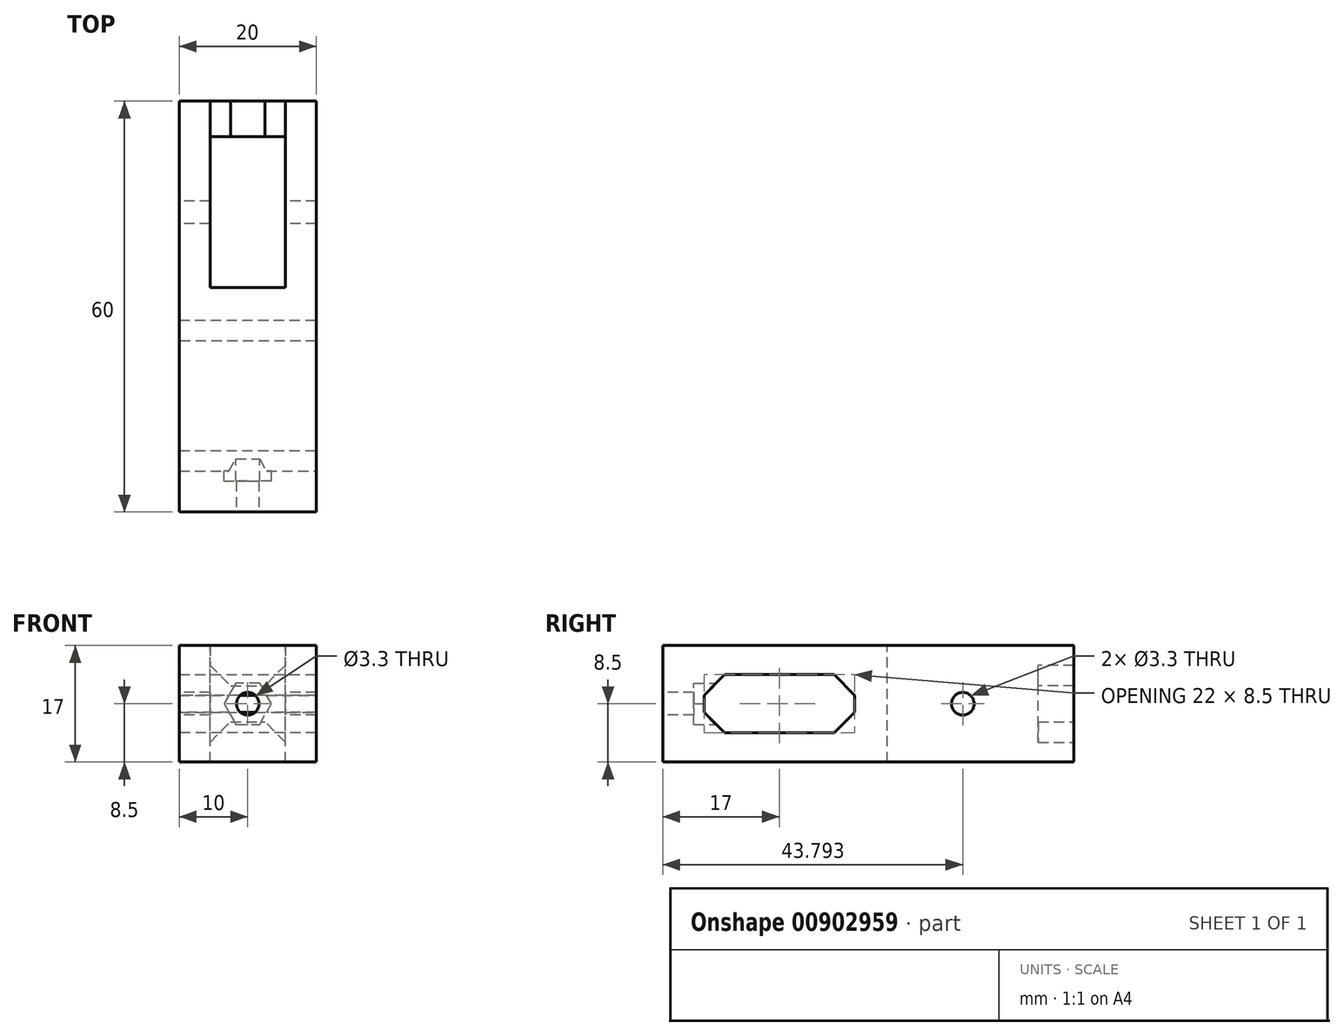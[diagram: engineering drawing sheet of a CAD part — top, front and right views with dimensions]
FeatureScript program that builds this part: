
annotation { "Feature Type Name" : "Feature", "Feature Type Description" : "" }
export const myFeature = defineFeature(function(context is Context, id is Id, definition is map)
    precondition{}
    {
        {
            var Q0;
            Q0=qCreatedBy(makeId("Right.planeOp"),FACE);
            var sketch = newSketch(context, id + "F0", { "sketchPlane" : qUnion([Q0])});
            skLineSegment(sketch, "E0.bottom", {"start": v(30, -8.5) * mm, "end": v(-30, -8.5) * mm});
            skLineSegment(sketch, "E0.top", {"start": v(30, 8.5) * mm, "end": v(-30, 8.5) * mm});
            skLineSegment(sketch, "E0.left", {"start": v(30, -8.5) * mm, "end": v(30, 8.5) * mm});
            skLineSegment(sketch, "E0.right", {"start": v(-30, -8.5) * mm, "end": v(-30, 8.5) * mm});
            skPoint(sketch, "E0.middle", {"position": v(0, 0) * mm});
            skSolve(sketch);
        }
        {
            var Q0;
            Q0 = qSketchRegion(id + "F0", true);
            extrude(context, id + "F1", {"entities" : qUnion([Q0]), "endBound" : BoundingType.SYMMETRIC, "depth" : 20 * mm, "offsetDistance" : 25 * mm});
        }
        {
            var Q0;
            Q0=makeQuery(id+"F1.opExtrude","CAP_FACE",FACE,{"disambiguationData":[OSD([sQuery(id+"F0.wireOp",EDGE,"E0.bottom"),sQuery(id+"F0.wireOp",EDGE,"E0.top"),sQuery(id+"F0.wireOp",EDGE,"E0.left"),sQuery(id+"F0.wireOp",EDGE,"E0.right")])],"isStart":false});
            var sketch = newSketch(context, id + "F2", { "sketchPlane" : qUnion([Q0])});
            skLineSegment(sketch, "E1.bottom", {"start": v(-2, -4.25) * mm, "end": v(-24, -4.25) * mm});
            skLineSegment(sketch, "E1.top", {"start": v(-2, 4.25) * mm, "end": v(-24, 4.25) * mm});
            skLineSegment(sketch, "E1.left", {"start": v(-2, -4.25) * mm, "end": v(-2, 4.25) * mm});
            skLineSegment(sketch, "E1.right", {"start": v(-24, -4.25) * mm, "end": v(-24, 4.25) * mm});
            skPoint(sketch, "E1.middle", {"position": v(-13, 0) * mm});
            skSolve(sketch);
        }
        {
            var Q0;
            Q0 = qSketchRegion(id + "F2", true);
            extrude(context, id + "F3", {"entities" : qUnion([Q0]), "operationType" : NewBodyOperationType.REMOVE, "oppositeDirection" : true, "depth" : 25 * mm, "offsetDistance" : 25 * mm});
        }
        {
            var Q0;
            Q0=makeQuery(id+"F1.opExtrude","SWEPT_FACE",FACE,{"disambiguationData":[OSD([sQuery(id+"F0.wireOp",EDGE,"E0.top")])]});
            var sketch = newSketch(context, id + "F4", { "sketchPlane" : qUnion([Q0])});
            skLineSegment(sketch, "E2.bottom", {"start": v(5.5, 24.8) * mm, "end": v(-5.5, 24.8) * mm});
            skLineSegment(sketch, "E2.top", {"start": v(5.5, 2.8) * mm, "end": v(-5.5, 2.8) * mm});
            skLineSegment(sketch, "E2.left", {"start": v(5.5, 24.8) * mm, "end": v(5.5, 2.8) * mm});
            skLineSegment(sketch, "E2.right", {"start": v(-5.5, 24.8) * mm, "end": v(-5.5, 2.8) * mm});
            skPoint(sketch, "E2.middle", {"position": v(0, 13.8) * mm});
            skSolve(sketch);
        }
        {
            var Q0;
            Q0 = qSketchRegion(id + "F4", true);
            extrude(context, id + "F5", {"entities" : qUnion([Q0]), "operationType" : NewBodyOperationType.REMOVE, "oppositeDirection" : true, "depth" : 25 * mm, "offsetDistance" : 25 * mm});
        }
        {
            var Q0;
            Q0=makeQuery(id+"F1.opExtrude","CAP_FACE",FACE,{"disambiguationData":[OSD([sQuery(id+"F0.wireOp",EDGE,"E0.bottom"),sQuery(id+"F0.wireOp",EDGE,"E0.top"),sQuery(id+"F0.wireOp",EDGE,"E0.left"),sQuery(id+"F0.wireOp",EDGE,"E0.right")])],"isStart":true});
            var sketch = newSketch(context, id + "F6", { "sketchPlane" : qUnion([Q0])});
            skPoint(sketch, "E3.0", {"position": v(-2.8, 8.5) * mm});
            skPoint(sketch, "E4.0", {"position": v(-24.8, -8.5) * mm});
            skLineSegment(sketch, "E5", {"start": v(-2.8, 8.5) * mm, "end": v(-24.8, -8.5) * mm, "construction": true});
            skCircle(sketch, "E6", {"center": v(-13.8, 0) * mm, "radius": 1.65 * mm});
            skSolve(sketch);
        }
        {
            var Q0;
            Q0 = qSketchRegion(id + "F6", true);
            extrude(context, id + "F7", {"entities" : qUnion([Q0]), "operationType" : NewBodyOperationType.REMOVE, "oppositeDirection" : true, "depth" : 25 * mm, "offsetDistance" : 25 * mm});
        }
        {
            var Q0;
            Q0=makeQuery(id+"F1.opExtrude","SWEPT_FACE",FACE,{"disambiguationData":[OSD([sQuery(id+"F0.wireOp",EDGE,"E0.left")])]});
            var sketch = newSketch(context, id + "F8", { "sketchPlane" : qUnion([Q0])});
            skPoint(sketch, "E7.0", {"position": v(5.5, 8.5) * mm});
            skPoint(sketch, "E8.0", {"position": v(-5.5, 8.5) * mm});
            skLineSegment(sketch, "E9.bottom", {"start": v(5.5, 8.5) * mm, "end": v(-5.5, 8.5) * mm});
            skLineSegment(sketch, "E9.top", {"start": v(5.5, 2.62) * mm, "end": v(-5.5, 2.62) * mm});
            skLineSegment(sketch, "E9.left", {"start": v(5.5, 8.5) * mm, "end": v(5.5, 2.62) * mm});
            skLineSegment(sketch, "E9.right", {"start": v(-5.5, 8.5) * mm, "end": v(-5.5, 2.62) * mm});
            skLineSegment(sketch, "E10.MirrorCS", {"start": v(5.5, -2.62) * mm, "end": v(-5.5, -2.62) * mm});
            skLineSegment(sketch, "E11.MirrorCS", {"start": v(5.5, -8.5) * mm, "end": v(5.5, -2.62) * mm});
            skPoint(sketch, "E12.MirrorP", {"position": v(-5.5, -8.5) * mm});
            skLineSegment(sketch, "E13.MirrorCS", {"start": v(5.5, -8.5) * mm, "end": v(-5.5, -8.5) * mm});
            skLineSegment(sketch, "E14.MirrorCS", {"start": v(-5.5, -8.5) * mm, "end": v(-5.5, -2.62) * mm});
            skPoint(sketch, "E15.MirrorP", {"position": v(5.5, -8.5) * mm});
            skSolve(sketch);
        }
        {
            var Q0;
            Q0 = qSketchRegion(id + "F8", true);
            extrude(context, id + "F9", {"entities" : qUnion([Q0]), "operationType" : NewBodyOperationType.REMOVE, "oppositeDirection" : true, "depth" : 6 * mm, "offsetDistance" : 25 * mm});
        }
        {
            var Q0;
            Q0=makeQuery(id+"F9.boolean.opBoolean","COPY",EDGE,{"derivedFrom":makeQuery(id+"F9.opExtrude","SWEPT_EDGE",EDGE,{"disambiguationData":[OSD([sQuery(id+"F8.wireOp",EDGE,"E9.top"),sQuery(id+"F8.wireOp",EDGE,"E9.left")])]})});
            var Q1;
            Q1=makeQuery(id+"F9.boolean.opBoolean","COPY",EDGE,{"derivedFrom":makeQuery(id+"F9.opExtrude","SWEPT_EDGE",EDGE,{"disambiguationData":[OSD([sQuery(id+"F8.wireOp",EDGE,"E9.top"),sQuery(id+"F8.wireOp",EDGE,"E9.right")])]})});
            var Q2;
            Q2=makeQuery(id+"F9.boolean.opBoolean","COPY",EDGE,{"derivedFrom":makeQuery(id+"F9.opExtrude","SWEPT_EDGE",EDGE,{"disambiguationData":[OSD([sQuery(id+"F8.wireOp",EDGE,"E10.MirrorCS"),sQuery(id+"F8.wireOp",EDGE,"E14.MirrorCS")])]})});
            var Q3;
            Q3=makeQuery(id+"F9.boolean.opBoolean","COPY",EDGE,{"derivedFrom":makeQuery(id+"F9.opExtrude","SWEPT_EDGE",EDGE,{"disambiguationData":[OSD([sQuery(id+"F8.wireOp",EDGE,"E10.MirrorCS"),sQuery(id+"F8.wireOp",EDGE,"E11.MirrorCS")])]})});
            chamfer(context, id + "F10", {"entities" : qUnion([Q0, Q1, Q2, Q3]), "width" : 3 * mm, "tangentPropagation" : true});
        }
        {
            var Q0;
            Q0=makeQuery(id+"F3.boolean.opBoolean","COPY",FACE,{"derivedFrom":makeQuery(id+"F3.opExtrude","SWEPT_FACE",FACE,{"disambiguationData":[OSD([sQuery(id+"F2.wireOp",EDGE,"E1.right")])]})});
            var sketch = newSketch(context, id + "F11", { "sketchPlane" : qUnion([Q0])});
            skLineSegment(sketch, "E16", {"start": v(10, 4.25) * mm, "end": v(-10, -4.25) * mm, "construction": true});
            skCircle(sketch, "E17.cCircle", {"center": v(0, 0) * mm, "radius": 3 * mm, "construction": true});
            skLineSegment(sketch, "E17.0", {"start": v(-3.46, 0) * mm, "end": v(-1.73, 3) * mm});
            skLineSegment(sketch, "E17.1", {"start": v(-1.73, 3) * mm, "end": v(1.73, 3) * mm});
            skLineSegment(sketch, "E17.2", {"start": v(1.73, 3) * mm, "end": v(3.46, 0) * mm});
            skLineSegment(sketch, "E17.3", {"start": v(3.46, 0) * mm, "end": v(1.73, -3) * mm});
            skLineSegment(sketch, "E17.4", {"start": v(1.73, -3) * mm, "end": v(-1.73, -3) * mm});
            skLineSegment(sketch, "E17.5", {"start": v(-1.73, -3) * mm, "end": v(-3.46, 0) * mm});
            skPoint(sketch, "E17.0.midPoint", {"position": v(-2.6, 1.5) * mm});
            skSolve(sketch);
        }
        {
            var Q0;
            Q0 = qSketchRegion(id + "F11", true);
            extrude(context, id + "F12", {"entities" : qUnion([Q0]), "operationType" : NewBodyOperationType.REMOVE, "endBound" : BoundingType.SYMMETRIC, "oppositeDirection" : true, "depth" : 3 * mm, "offsetDistance" : 25 * mm});
        }
        {
            var Q0;
            Q0=makeQuery(id+"F1.opExtrude","SWEPT_FACE",FACE,{"disambiguationData":[OSD([sQuery(id+"F0.wireOp",EDGE,"E0.right")])]});
            var sketch = newSketch(context, id + "F13", { "sketchPlane" : qUnion([Q0])});
            skLineSegment(sketch, "E18", {"start": v(10, 8.5) * mm, "end": v(-10, -8.5) * mm, "construction": true});
            skCircle(sketch, "E19", {"center": v(0, 0) * mm, "radius": 1.65 * mm});
            skSolve(sketch);
        }
        {
            var Q0;
            Q0 = qSketchRegion(id + "F13", true);
            extrude(context, id + "F14", {"entities" : qUnion([Q0]), "operationType" : NewBodyOperationType.REMOVE, "oppositeDirection" : true, "depth" : 10 * mm, "offsetDistance" : 25 * mm});
        }
        {
            var Q0;
            Q0=makeQuery(id+"F3.boolean.opBoolean","COPY",EDGE,{"derivedFrom":makeQuery(id+"F3.opExtrude","SWEPT_EDGE",EDGE,{"disambiguationData":[OSD([sQuery(id+"F2.wireOp",EDGE,"E1.top"),sQuery(id+"F2.wireOp",EDGE,"E1.left")])]})});
            var Q1;
            Q1=makeQuery(id+"F3.boolean.opBoolean","COPY",EDGE,{"derivedFrom":makeQuery(id+"F3.opExtrude","SWEPT_EDGE",EDGE,{"disambiguationData":[OSD([sQuery(id+"F2.wireOp",EDGE,"E1.bottom"),sQuery(id+"F2.wireOp",EDGE,"E1.left")])]})});
            var Q2;
            Q2=makeQuery(id+"F3.boolean.opBoolean","COPY",EDGE,{"derivedFrom":makeQuery(id+"F3.opExtrude","SWEPT_EDGE",EDGE,{"disambiguationData":[OSD([sQuery(id+"F2.wireOp",EDGE,"E1.bottom"),sQuery(id+"F2.wireOp",EDGE,"E1.right")])]})});
            var Q3;
            Q3=makeQuery(id+"F3.boolean.opBoolean","COPY",EDGE,{"derivedFrom":makeQuery(id+"F3.opExtrude","SWEPT_EDGE",EDGE,{"disambiguationData":[OSD([sQuery(id+"F2.wireOp",EDGE,"E1.top"),sQuery(id+"F2.wireOp",EDGE,"E1.right")])]})});
            chamfer(context, id + "F15", {"entities" : qUnion([Q0, Q1, Q2, Q3]), "width" : 3 * mm, "tangentPropagation" : true});
        }
    });
